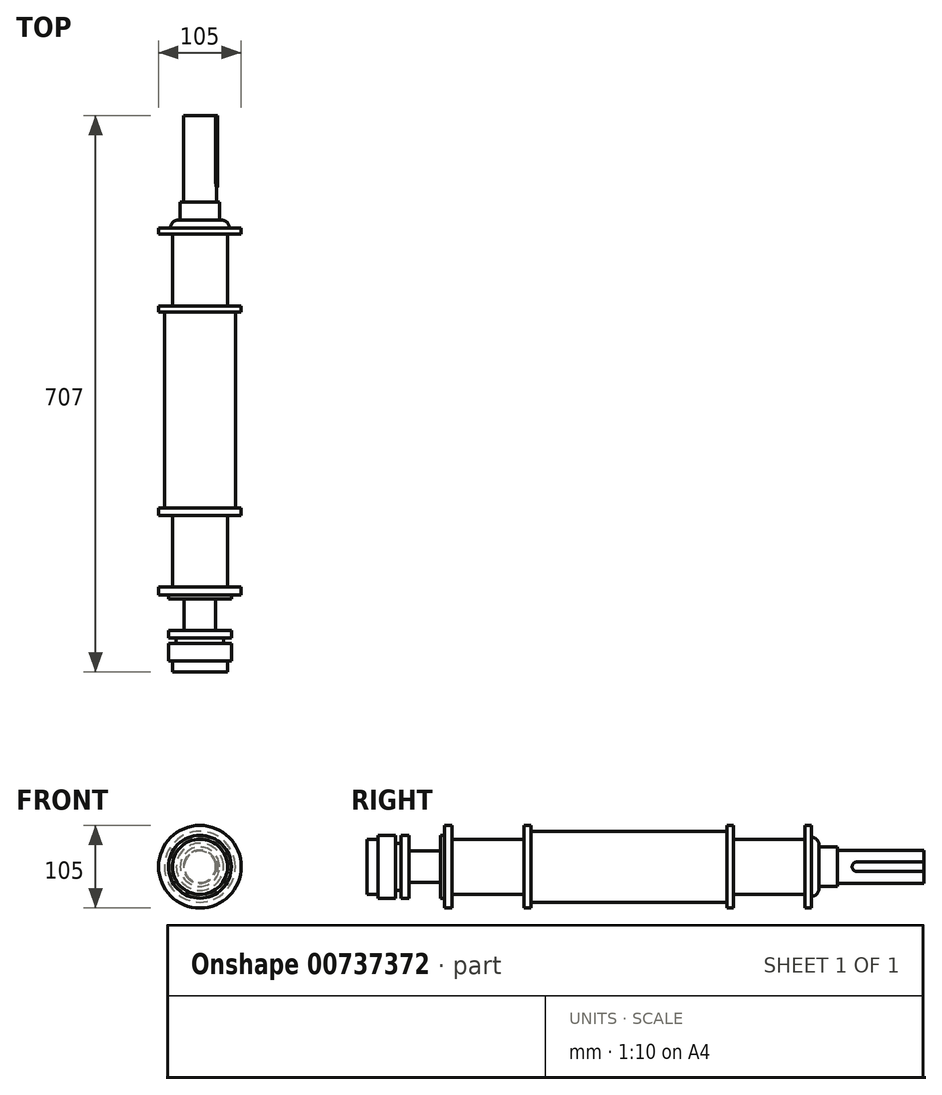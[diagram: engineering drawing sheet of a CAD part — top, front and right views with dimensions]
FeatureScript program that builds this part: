
annotation { "Feature Type Name" : "Feature", "Feature Type Description" : "" }
export const myFeature = defineFeature(function(context is Context, id is Id, definition is map)
    precondition{}
    {
        {
            var Q0;
            Q0=qCreatedBy(makeId("Front.planeOp"),FACE);
            var sketch = newSketch(context, id + "F0", { "sketchPlane" : qUnion([Q0])});
            skCircle(sketch, "E0", {"center": v(0, 0) * mm, "radius": 21 * mm});
            skSolve(sketch);
        }
        {
            var Q0;
            Q0=makeQuery(id+"F0.imprint","IMPRINT",FACE,{"disambiguationData":[TD([[makeQuery(id+"F0.imprint","IMPRINT",EDGE,{"derivedFrom":sQuery(id+"F0.wireOp",EDGE,"E0")}),1.0]])]});
            extrude(context, id + "F1", {"entities" : qUnion([Q0]), "depth" : 110 * mm, "offsetDistance" : 25 * mm});
        }
        {
            var Q0;
            Q0=qCreatedBy(makeId("Right.planeOp"),FACE);
            var sketch = newSketch(context, id + "F2", { "sketchPlane" : qUnion([Q0])});
            skLineSegment(sketch, "E1.bottom", {"start": v(0, 6) * mm, "end": v(-85, 6) * mm});
            skLineSegment(sketch, "E1.top", {"start": v(0, -6) * mm, "end": v(-85, -6) * mm});
            skLineSegment(sketch, "E1.left", {"start": v(0, 6) * mm, "end": v(0, -6) * mm});
            skArc(sketch, "E2", {"start": v(-85, 6) * mm, "mid": v(-91, 0) * mm, "end": v(-85, -6) * mm});
            skSolve(sketch);
        }
        {
            var Q0;
            Q0 = qSketchRegion(id + "F2", true);
            extrude(context, id + "F3", {"entities" : qUnion([Q0]), "operationType" : NewBodyOperationType.ADD, "depth" : (45 / 2) * mm, "offsetDistance" : 25 * mm});
        }
        {
            var Q0;
            Q0=makeQuery(id+"F1.opExtrude","CAP_FACE",FACE,{"disambiguationData":[OSD([sQuery(id+"F0.wireOp",EDGE,"E0")])],"isStart":false});
            var sketch = newSketch(context, id + "F4", { "sketchPlane" : qUnion([Q0])});
            skCircle(sketch, "E3", {"center": v(0, 0) * mm, "radius": 25 * mm});
            skSolve(sketch);
        }
        {
            var Q0;
            Q0 = qSketchRegion(id + "F4", true);
            extrude(context, id + "F5", {"entities" : qUnion([Q0]), "operationType" : NewBodyOperationType.ADD, "depth" : 23 * mm, "offsetDistance" : 25 * mm});
        }
        {
            var Q0;
            Q0=makeQuery(id+"F5.opExtrude","CAP_FACE",FACE,{"disambiguationData":[OSD([sQuery(id+"F4.wireOp",EDGE,"E3")])],"isStart":false});
            var sketch = newSketch(context, id + "F6", { "sketchPlane" : qUnion([Q0])});
            skCircle(sketch, "E4", {"center": v(0, 0) * mm, "radius": 37.5 * mm});
            skSolve(sketch);
        }
        {
            var Q0;
            Q0 = qSketchRegion(id + "F6", true);
            extrude(context, id + "F7", {"entities" : qUnion([Q0]), "operationType" : NewBodyOperationType.ADD, "depth" : 10 * mm, "offsetDistance" : 25 * mm});
        }
        {
            var Q0;
            Q0=makeQuery(id+"F7.opExtrude","CAP_EDGE",EDGE,{"disambiguationData":[OSD([sQuery(id+"F6.wireOp",EDGE,"E4")])],"isStart":true});
            fillet(context, id + "F8", {"entities" : qUnion([Q0]), "radius" : 10 * mm, "tangentPropagation" : true, "allowEdgeOverflow" : false});
        }
        {
            var Q0;
            Q0=makeQuery(id+"F7.opExtrude","CAP_FACE",FACE,{"disambiguationData":[OSD([sQuery(id+"F6.wireOp",EDGE,"E4")])],"isStart":false});
            var sketch = newSketch(context, id + "F9", { "sketchPlane" : qUnion([Q0])});
            skCircle(sketch, "E5", {"center": v(0, 0) * mm, "radius": 52.5 * mm});
            skSolve(sketch);
        }
        {
            var Q0;
            Q0=makeQuery(id+"F9.imprint","IMPRINT",FACE,{"disambiguationData":[TD([[makeQuery(id+"F9.imprint","IMPRINT",EDGE,{"derivedFrom":sQuery(id+"F9.wireOp",EDGE,"E5")}),1.0]])]});
            var Q1;
            {var subQ0=sQuery(id+"F6.wireOp",EDGE,"E4");Q1=makeQuery(id+"F9.imprint","IMPRINT",FACE,{"disambiguationData":[TD([[makeQuery(id+"F9.imprint","IMPRINT",EDGE,{"derivedFrom":makeQuery(id+"F8.opFillet","BLEND_EDGE",EDGE,{"blendedFrom":[makeQuery(id+"F7.opExtrude","CAP_EDGE",EDGE,{"disambiguationData":[OSD([subQ0])],"isStart":true}),makeQuery(id+"F7.opExtrude","CAP_FACE",FACE,{"disambiguationData":[OSD([subQ0])],"isStart":false})],"blendedInto":[makeQuery(id+"F7.opExtrude","CAP_FACE",FACE,{"disambiguationData":[OSD([subQ0])],"isStart":false})]})}),1.0]])]});}
            extrude(context, id + "F10", {"entities" : qUnion([Q0, Q1]), "operationType" : NewBodyOperationType.ADD, "depth" : 8 * mm, "offsetDistance" : 25 * mm});
        }
        {
            var Q0;
            Q0=makeQuery(id+"F10.opExtrude","CAP_FACE",FACE,{"disambiguationData":[OSD([sQuery(id+"F9.wireOp",EDGE,"E5")])],"isStart":false});
            var sketch = newSketch(context, id + "F11", { "sketchPlane" : qUnion([Q0])});
            skCircle(sketch, "E6", {"center": v(0, 0) * mm, "radius": 35 * mm});
            skSolve(sketch);
        }
        {
            var Q0;
            Q0=makeQuery(id+"F11.imprint","IMPRINT",FACE,{"disambiguationData":[TD([[makeQuery(id+"F11.imprint","IMPRINT",EDGE,{"derivedFrom":sQuery(id+"F11.wireOp",EDGE,"E6")}),1.0]])]});
            extrude(context, id + "F12", {"entities" : qUnion([Q0]), "operationType" : NewBodyOperationType.ADD, "depth" : 91 * mm, "offsetDistance" : 25 * mm});
        }
        {
            var Q0;
            Q0=makeQuery(id+"F12.opExtrude","CAP_FACE",FACE,{"disambiguationData":[OSD([sQuery(id+"F11.wireOp",EDGE,"E6")])],"isStart":false});
            var sketch = newSketch(context, id + "F13", { "sketchPlane" : qUnion([Q0])});
            skCircle(sketch, "E7.0", {"center": v(0, 0) * mm, "radius": 52.5 * mm});
            skSolve(sketch);
        }
        {
            var Q0;
            Q0 = qSketchRegion(id + "F13", true);
            extrude(context, id + "F14", {"entities" : qUnion([Q0]), "operationType" : NewBodyOperationType.ADD, "depth" : 8 * mm, "offsetDistance" : 25 * mm});
        }
        {
            var Q0;
            Q0=makeQuery(id+"F14.opExtrude","CAP_FACE",FACE,{"disambiguationData":[OSD([sQuery(id+"F13.wireOp",EDGE,"E7.0")])],"isStart":false});
            var sketch = newSketch(context, id + "F15", { "sketchPlane" : qUnion([Q0])});
            skCircle(sketch, "E8", {"center": v(0, 0) * mm, "radius": 45 * mm});
            skSolve(sketch);
        }
        {
            var Q0;
            Q0=makeQuery(id+"F15.imprint","IMPRINT",FACE,{"disambiguationData":[TD([[makeQuery(id+"F15.imprint","IMPRINT",EDGE,{"derivedFrom":sQuery(id+"F15.wireOp",EDGE,"E8")}),1.0]])]});
            extrude(context, id + "F16", {"entities" : qUnion([Q0]), "operationType" : NewBodyOperationType.ADD, "depth" : (267 - 18) * mm, "offsetDistance" : 25 * mm});
        }
        {
            var Q0;
            Q0=makeQuery(id+"F16.opExtrude","CAP_FACE",FACE,{"disambiguationData":[OSD([sQuery(id+"F15.wireOp",EDGE,"E8")])],"isStart":false});
            var sketch = newSketch(context, id + "F17", { "sketchPlane" : qUnion([Q0])});
            skCircle(sketch, "E9.0", {"center": v(0, 0) * mm, "radius": 52.5 * mm});
            skSolve(sketch);
        }
        {
            var Q0;
            Q0 = qSketchRegion(id + "F17", true);
            extrude(context, id + "F18", {"entities" : qUnion([Q0]), "operationType" : NewBodyOperationType.ADD, "depth" : 9 * mm, "offsetDistance" : 25 * mm});
        }
        {
            var Q0;
            Q0=makeQuery(id+"F18.opExtrude","CAP_FACE",FACE,{"disambiguationData":[OSD([sQuery(id+"F17.wireOp",EDGE,"E9.0")])],"isStart":false});
            var sketch = newSketch(context, id + "F19", { "sketchPlane" : qUnion([Q0])});
            skCircle(sketch, "E10", {"center": v(0, 0) * mm, "radius": 35 * mm});
            skSolve(sketch);
        }
        {
            var Q0;
            Q0=makeQuery(id+"F19.imprint","IMPRINT",FACE,{"disambiguationData":[TD([[makeQuery(id+"F19.imprint","IMPRINT",EDGE,{"derivedFrom":sQuery(id+"F19.wireOp",EDGE,"E10")}),1.0]])]});
            extrude(context, id + "F20", {"entities" : qUnion([Q0]), "operationType" : NewBodyOperationType.ADD, "depth" : 91 * mm, "offsetDistance" : 25 * mm});
        }
        {
            var Q0;
            Q0=makeQuery(id+"F20.opExtrude","CAP_FACE",FACE,{"disambiguationData":[OSD([sQuery(id+"F19.wireOp",EDGE,"E10")])],"isStart":false});
            var sketch = newSketch(context, id + "F21", { "sketchPlane" : qUnion([Q0])});
            skCircle(sketch, "E11.0", {"center": v(0, 0) * mm, "radius": 52.5 * mm});
            skSolve(sketch);
        }
        {
            var Q0;
            Q0 = qSketchRegion(id + "F21", true);
            extrude(context, id + "F22", {"entities" : qUnion([Q0]), "operationType" : NewBodyOperationType.ADD, "depth" : 10 * mm, "offsetDistance" : 25 * mm});
        }
        {
            var Q0;
            Q0=makeQuery(id+"F22.opExtrude","CAP_FACE",FACE,{"disambiguationData":[OSD([sQuery(id+"F21.wireOp",EDGE,"E11.0")])],"isStart":false});
            var sketch = newSketch(context, id + "F23", { "sketchPlane" : qUnion([Q0])});
            skCircle(sketch, "E12", {"center": v(0, 0) * mm, "radius": 40 * mm});
            skSolve(sketch);
        }
        {
            var Q0;
            Q0=makeQuery(id+"F23.imprint","IMPRINT",FACE,{"disambiguationData":[TD([[makeQuery(id+"F23.imprint","IMPRINT",EDGE,{"derivedFrom":sQuery(id+"F23.wireOp",EDGE,"E12")}),1.0]])]});
            extrude(context, id + "F24", {"entities" : qUnion([Q0]), "operationType" : NewBodyOperationType.ADD, "depth" : 5 * mm, "offsetDistance" : 25 * mm});
        }
        {
            var Q0;
            Q0=makeQuery(id+"F24.opExtrude","CAP_FACE",FACE,{"disambiguationData":[OSD([sQuery(id+"F23.wireOp",EDGE,"E12")])],"isStart":false});
            var sketch = newSketch(context, id + "F25", { "sketchPlane" : qUnion([Q0])});
            skCircle(sketch, "E13", {"center": v(0, 0) * mm, "radius": 20 * mm});
            skSolve(sketch);
        }
        {
            var Q0;
            Q0=makeQuery(id+"F25.imprint","IMPRINT",FACE,{"disambiguationData":[TD([[makeQuery(id+"F25.imprint","IMPRINT",EDGE,{"derivedFrom":sQuery(id+"F25.wireOp",EDGE,"E13")}),1.0]])]});
            extrude(context, id + "F26", {"entities" : qUnion([Q0]), "operationType" : NewBodyOperationType.ADD, "depth" : 40 * mm, "offsetDistance" : 25 * mm});
        }
        {
            var Q0;
            Q0=makeQuery(id+"F26.opExtrude","CAP_FACE",FACE,{"disambiguationData":[OSD([sQuery(id+"F25.wireOp",EDGE,"E13")])],"isStart":false});
            var sketch = newSketch(context, id + "F27", { "sketchPlane" : qUnion([Q0])});
            skCircle(sketch, "E14.0", {"center": v(0, 0) * mm, "radius": 40 * mm});
            skSolve(sketch);
        }
        {
            var Q0;
            Q0 = qSketchRegion(id + "F27", true);
            extrude(context, id + "F28", {"entities" : qUnion([Q0]), "operationType" : NewBodyOperationType.ADD, "depth" : 10 * mm, "offsetDistance" : 25 * mm});
        }
        {
            var Q0;
            Q0=makeQuery(id+"F28.opExtrude","CAP_FACE",FACE,{"disambiguationData":[OSD([sQuery(id+"F27.wireOp",EDGE,"E14.0")])],"isStart":false});
            var sketch = newSketch(context, id + "F29", { "sketchPlane" : qUnion([Q0])});
            skCircle(sketch, "E15", {"center": v(0, 0) * mm, "radius": 30 * mm});
            skSolve(sketch);
        }
        {
            var Q0;
            Q0=makeQuery(id+"F29.imprint","IMPRINT",FACE,{"disambiguationData":[TD([[makeQuery(id+"F29.imprint","IMPRINT",EDGE,{"derivedFrom":sQuery(id+"F29.wireOp",EDGE,"E15")}),1.0]])]});
            extrude(context, id + "F30", {"entities" : qUnion([Q0]), "operationType" : NewBodyOperationType.ADD, "depth" : 7 * mm, "offsetDistance" : 25 * mm});
        }
        {
            var Q0;
            Q0=makeQuery(id+"F30.opExtrude","CAP_FACE",FACE,{"disambiguationData":[OSD([sQuery(id+"F29.wireOp",EDGE,"E15")])],"isStart":false});
            var sketch = newSketch(context, id + "F31", { "sketchPlane" : qUnion([Q0])});
            skCircle(sketch, "E16.0", {"center": v(0, 0) * mm, "radius": 40 * mm});
            skSolve(sketch);
        }
        {
            var Q0;
            Q0 = qSketchRegion(id + "F31", true);
            extrude(context, id + "F32", {"entities" : qUnion([Q0]), "operationType" : NewBodyOperationType.ADD, "depth" : 22 * mm, "offsetDistance" : 25 * mm});
        }
        {
            var Q0;
            Q0=makeQuery(id+"F32.opExtrude","CAP_FACE",FACE,{"disambiguationData":[OSD([sQuery(id+"F31.wireOp",EDGE,"E16.0")])],"isStart":false});
            var sketch = newSketch(context, id + "F33", { "sketchPlane" : qUnion([Q0])});
            skCircle(sketch, "E17", {"center": v(0, 0) * mm, "radius": 35 * mm});
            skSolve(sketch);
        }
        {
            var Q0;
            Q0=makeQuery(id+"F33.imprint","IMPRINT",FACE,{"disambiguationData":[TD([[makeQuery(id+"F33.imprint","IMPRINT",EDGE,{"derivedFrom":sQuery(id+"F33.wireOp",EDGE,"E17")}),1.0]])]});
            extrude(context, id + "F34", {"entities" : qUnion([Q0]), "operationType" : NewBodyOperationType.ADD, "depth" : 14 * mm, "offsetDistance" : 25 * mm});
        }
    });
